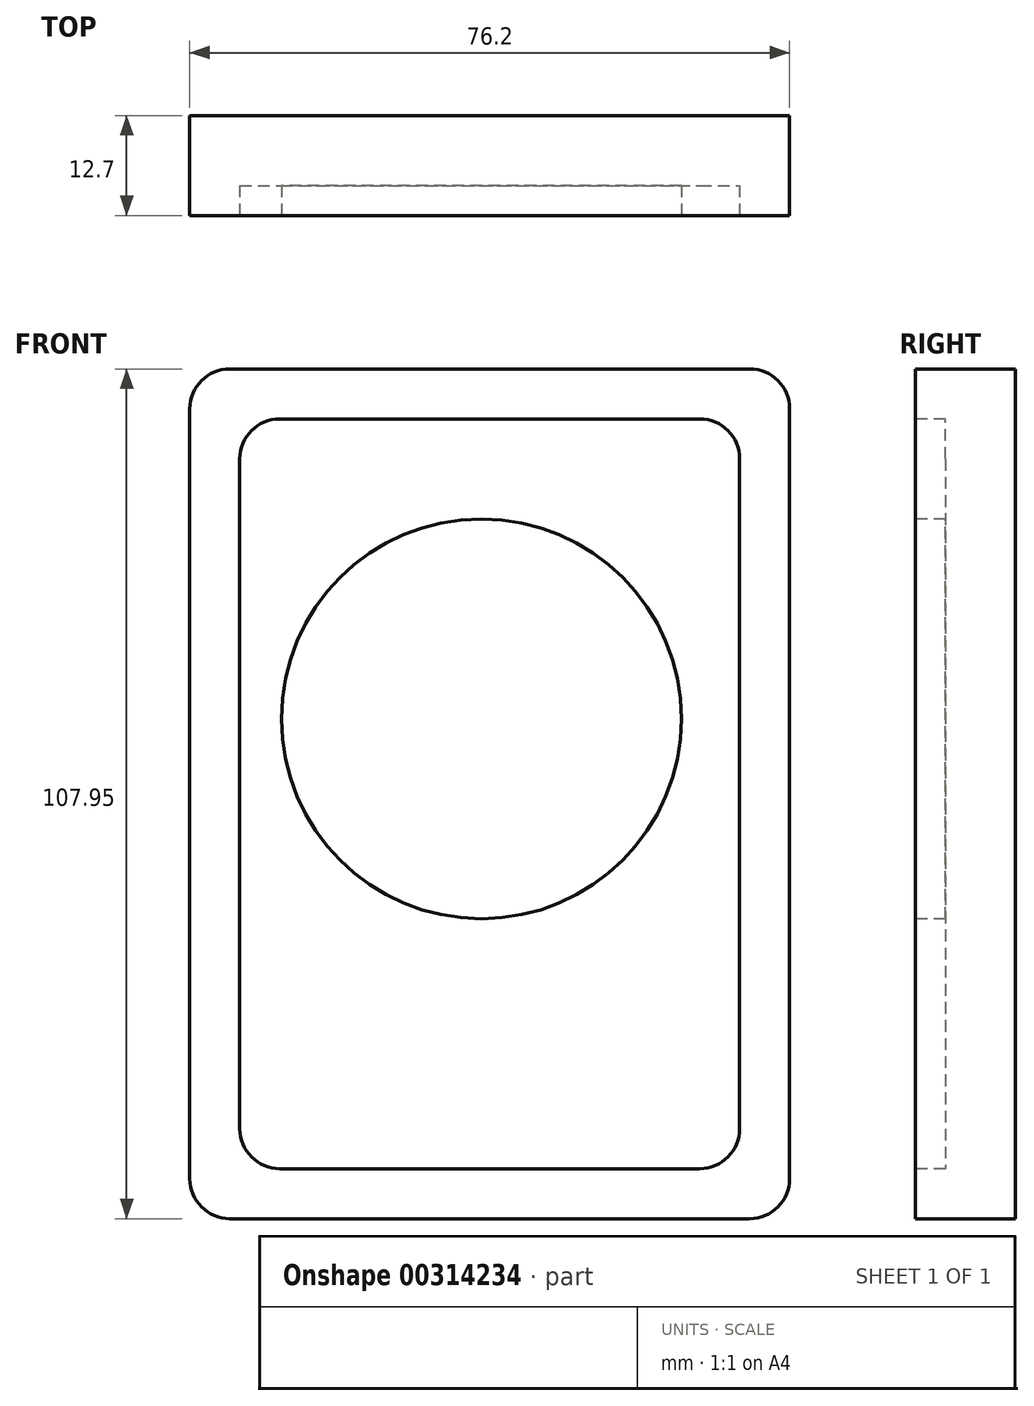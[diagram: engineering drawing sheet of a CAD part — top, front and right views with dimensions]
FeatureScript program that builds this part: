
annotation { "Feature Type Name" : "Feature", "Feature Type Description" : "" }
export const myFeature = defineFeature(function(context is Context, id is Id, definition is map)
    precondition{}
    {
        {
            var Q0;
            Q0=qCreatedBy(makeId("Front.planeOp"),FACE);
            var sketch = newSketch(context, id + "F0", { "sketchPlane" : qUnion([Q0])});
            skLineSegment(sketch, "E0.bottom", {"start": v(-47.14, 27.78) * mm, "end": v(29.06, 27.78) * mm});
            skLineSegment(sketch, "E0.top", {"start": v(-47.14, -80.17) * mm, "end": v(29.06, -80.17) * mm});
            skLineSegment(sketch, "E0.left", {"start": v(-47.14, 27.78) * mm, "end": v(-47.14, -80.17) * mm});
            skLineSegment(sketch, "E0.right", {"start": v(29.06, 27.78) * mm, "end": v(29.06, -80.17) * mm});
            skSolve(sketch);
        }
        {
            var Q0;
            Q0=makeQuery(id+"F0.imprint","IMPRINT",FACE,{"disambiguationData":[TD([[makeQuery(id+"F0.imprint","IMPRINT",EDGE,{"derivedFrom":sQuery(id+"F0.wireOp",EDGE,"E0.bottom")}),-1.0]])]});
            extrude(context, id + "F1", {"entities" : qUnion([Q0]), "depth" : 12.7 * mm});
        }
        {
            var Q0;
            Q0=makeQuery(id+"F1.opExtrude","SWEPT_EDGE",EDGE,{"disambiguationData":[OSD([sQuery(id+"F0.wireOp",EDGE,"E0.bottom"),sQuery(id+"F0.wireOp",EDGE,"E0.left")])]});
            var Q1;
            Q1=makeQuery(id+"F1.opExtrude","SWEPT_EDGE",EDGE,{"disambiguationData":[OSD([sQuery(id+"F0.wireOp",EDGE,"E0.bottom"),sQuery(id+"F0.wireOp",EDGE,"E0.right")])]});
            var Q2;
            Q2=makeQuery(id+"F1.opExtrude","SWEPT_EDGE",EDGE,{"disambiguationData":[OSD([sQuery(id+"F0.wireOp",EDGE,"E0.top"),sQuery(id+"F0.wireOp",EDGE,"E0.right")])]});
            var Q3;
            Q3=makeQuery(id+"F1.opExtrude","SWEPT_EDGE",EDGE,{"disambiguationData":[OSD([sQuery(id+"F0.wireOp",EDGE,"E0.top"),sQuery(id+"F0.wireOp",EDGE,"E0.left")])]});
            fillet(context, id + "F2", {"entities" : qUnion([Q0, Q1, Q2, Q3]), "radius" : 5.08 * mm, "tangentPropagation" : true, "allowEdgeOverflow" : false});
        }
        {
            var Q0;
            Q0=makeQuery(id+"F1.opExtrude","CAP_FACE",FACE,{"disambiguationData":[OSD([sQuery(id+"F0.wireOp",EDGE,"E0.bottom"),sQuery(id+"F0.wireOp",EDGE,"E0.top"),sQuery(id+"F0.wireOp",EDGE,"E0.left"),sQuery(id+"F0.wireOp",EDGE,"E0.right")])],"isStart":false});
            var sketch = newSketch(context, id + "F3", { "sketchPlane" : qUnion([Q0])});
            skLineSegment(sketch, "E1.bottom", {"start": v(-40.8, 21.43) * mm, "end": v(22.7, 21.43) * mm});
            skLineSegment(sketch, "E1.top", {"start": v(-40.8, -73.82) * mm, "end": v(22.7, -73.82) * mm});
            skLineSegment(sketch, "E1.left", {"start": v(-40.8, 21.43) * mm, "end": v(-40.8, -73.82) * mm});
            skLineSegment(sketch, "E1.right", {"start": v(22.7, 21.43) * mm, "end": v(22.7, -73.82) * mm});
            skCircle(sketch, "E2", {"center": v(-10.1, -16.67) * mm, "radius": 25.4 * mm});
            skSolve(sketch);
        }
        {
            var Q0;
            Q0 = qSketchRegion(id + "F3", true);
            extrude(context, id + "F4", {"entities" : qUnion([Q0]), "operationType" : NewBodyOperationType.REMOVE, "oppositeDirection" : true, "depth" : 3.8 * mm});
        }
        {
            var Q0;
            Q0=makeQuery(id+"F4.boolean.opBoolean","COPY",EDGE,{"derivedFrom":makeQuery(id+"F4.opExtrude","SWEPT_EDGE",EDGE,{"disambiguationData":[OSD([sQuery(id+"F3.wireOp",EDGE,"E1.bottom"),sQuery(id+"F3.wireOp",EDGE,"E1.left")])]})});
            var Q1;
            Q1=makeQuery(id+"F4.boolean.opBoolean","COPY",EDGE,{"derivedFrom":makeQuery(id+"F4.opExtrude","SWEPT_EDGE",EDGE,{"disambiguationData":[OSD([sQuery(id+"F3.wireOp",EDGE,"E1.bottom"),sQuery(id+"F3.wireOp",EDGE,"E1.right")])]})});
            var Q2;
            Q2=makeQuery(id+"F4.boolean.opBoolean","COPY",EDGE,{"derivedFrom":makeQuery(id+"F4.opExtrude","SWEPT_EDGE",EDGE,{"disambiguationData":[OSD([sQuery(id+"F3.wireOp",EDGE,"E1.top"),sQuery(id+"F3.wireOp",EDGE,"E1.right")])]})});
            var Q3;
            Q3=makeQuery(id+"F4.boolean.opBoolean","COPY",EDGE,{"derivedFrom":makeQuery(id+"F4.opExtrude","SWEPT_EDGE",EDGE,{"disambiguationData":[OSD([sQuery(id+"F3.wireOp",EDGE,"E1.top"),sQuery(id+"F3.wireOp",EDGE,"E1.left")])]})});
            fillet(context, id + "F5", {"entities" : qUnion([Q0, Q1, Q2, Q3]), "radius" : 5.08 * mm, "tangentPropagation" : true, "allowEdgeOverflow" : false});
        }
    });
